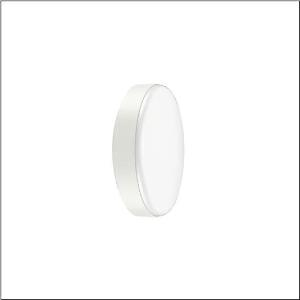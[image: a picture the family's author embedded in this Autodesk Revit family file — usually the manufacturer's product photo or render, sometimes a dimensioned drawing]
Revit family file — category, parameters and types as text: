
# Revit family: rondel_31_51wc10ma32as
name_source: partatom
category: Lighting Fixtures
units: mm (PartAtom-declared; Revit-internal decimal feet)

## family parameters
Cut with Voids When Loaded = No
Host = Face
Light Source = No
Part Type = Normal
Room Calculation Point = No
Round Connector Dimension = Use Diameter
Shared = No

## types (1)
- --- (1 x LED, 2450 lm, 20.4 W, 3000K)
    Apparent Load = 20 VA
    CIE Flux Codes = 44 75 94 94 100
    Color Rendering = 80
    Color Temperature = 3000K
    Default Elevation = 1800 mm
    Description = Rondel 31, wall and ceiling luminaire, primary optical cover: cover, of PC, opal, light emission: direct distribution, primary light characteristic: symmetric, installation type: surface-mounted, LED, rated luminous flux: 2.450lm, luminous efficacy: 120lm/W, light colour: 830, colour temperature: 3000K, with terminal, 3-pole, max. 2.5mm², mains connection: 220..240V, AC, 50/60Hz, rated input power: 20.5W, luminaire housing, of PC, traffic white (RAL 9016), diameter: 350mm, brightness and presence sensor, HF sensor, protection rating (complete): IP65, insulation class (complete): insulation class II (safety insulation), certification: CE, impact resistance: IK10, permissible operating ambient temperature: -20..+40°C, permissible storage temperature: -20..+60°C, packaging unit: 1 piece
    Height = 97 mm
    Lamp = 1 x LED
    Lamp Light Flux = 2450 lm
    Lamp Power = 20.4 W
    Lamp count = 1
    Length = 350 mm
    Luminous efficacy = 120 lm/W
    Manufacturer = Siteco
    ModVariant = No
    Model = 51WC10MA32AS
    Mounting Place = Ceiling
    Mounting Type = Surface mounted
    Number of Poles = 1
    OnlyDefault = Yes
    Power Factor = 1
    Product Name = Rondel 31
    Product group = wall and ceiling luminaire
    ProductGroupID = 302
    Protection Class = Protection class II
    Protection Degree = IP 65
    RLX_Detail_Level = 1
    RLX_Emergency_Light_Flux = 0 lm
    RLX_Emergency_Type = 0
    RLX_Emergency_Type_DB = No
    RlxData = <blob elided: 30397 chars, md5=07811b6e>
    Socket = socket
    Standby Power = 0 W
    System Light Flux = 2450 lm
    System Power = 20 W
    Type Comments = factory setting: luminous flux: 100 % | (ON | ON)
    Type Image = l_1007027.jpg
    URL = http://relux.com
    VarID = @adj_060099
    Voltage = 0 V
    Weight = 0.00 kg
    Width = 0 mm  [stored 0 ft]

note: [stored X ft] marks values corroborated as IEEE doubles in the binary element streams (Revit-internal decimal feet)

## geometry (parser evidence)
native form markers: Blend x4, Sweep x10
no freeform markers — native parametric forms only
